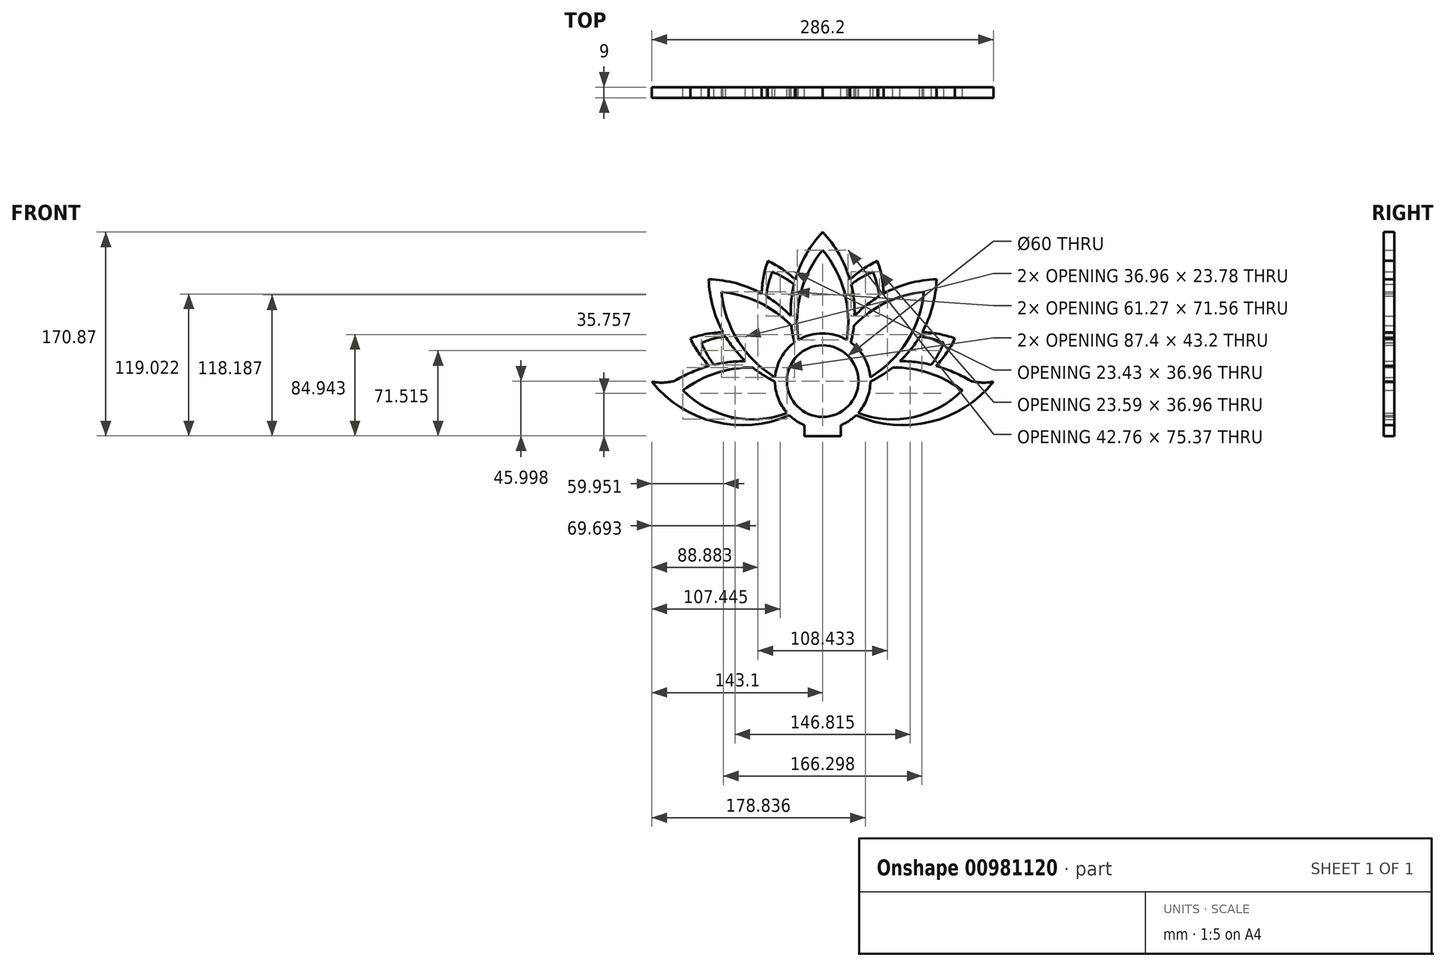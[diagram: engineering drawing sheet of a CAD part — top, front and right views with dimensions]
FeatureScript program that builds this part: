
annotation { "Feature Type Name" : "Feature", "Feature Type Description" : "" }
export const myFeature = defineFeature(function(context is Context, id is Id, definition is map)
    precondition{}
    {
        {
            var Q0;
            Q0=qCreatedBy(makeId("Front.planeOp"),FACE);
            var sketch = newSketch(context, id + "F0", { "sketchPlane" : qUnion([Q0])});
            skCircle(sketch, "E0", {"center": v(0, 0.48) * mm, "radius": 30 * mm});
            skArc(sketch, "E1", {"start": v(0, 110.35) * mm, "mid": v(-18.26, 74.85) * mm, "end": v(-20.24, 34.98) * mm});
            skArc(sketch, "E2", {"start": v(20.24, 34.98) * mm, "mid": v(18.26, 74.85) * mm, "end": v(0, 110.35) * mm});
            skArc(sketch, "E3", {"start": v(84.85, 75.2) * mm, "mid": v(53.03, 66.29) * mm, "end": v(26.22, 46.96) * mm});
            skArc(sketch, "E4", {"start": v(39.87, 3.64) * mm, "mid": v(70.81, 34.11) * mm, "end": v(84.85, 75.2) * mm});
            skArc(sketch, "E5", {"start": v(117.1, -7.36) * mm, "mid": v(89.45, 7.14) * mm, "end": v(58.57, 11.84) * mm});
            skArc(sketch, "E6", {"start": v(29.7, -26.31) * mm, "mid": v(76.2, -29.7) * mm, "end": v(117.1, -7.36) * mm});
            skArc(sketch, "E7", {"start": v(-58.57, 11.84) * mm, "mid": v(-89.45, 7.14) * mm, "end": v(-117.1, -7.36) * mm});
            skArc(sketch, "E8", {"start": v(-117.1, -7.36) * mm, "mid": v(-76.2, -29.7) * mm, "end": v(-29.7, -26.31) * mm});
            skArc(sketch, "E9", {"start": v(-84.85, 75.2) * mm, "mid": v(-70.81, 34.11) * mm, "end": v(-39.87, 3.64) * mm});
            skArc(sketch, "E10", {"start": v(-26.22, 46.96) * mm, "mid": v(-53.03, 66.29) * mm, "end": v(-84.85, 75.2) * mm});
            skArc(sketch, "E11", {"start": v(-101.63, 32.45) * mm, "mid": v(-96.95, 22.91) * mm, "end": v(-91.01, 14.1) * mm});
            skArc(sketch, "E12", {"start": v(-42.1, 91.98) * mm, "mid": v(-45.42, 81.99) * mm, "end": v(-47.37, 71.64) * mm});
            skArc(sketch, "E13", {"start": v(42.1, 91.98) * mm, "mid": v(32.66, 87.36) * mm, "end": v(23.94, 81.51) * mm});
            skArc(sketch, "E14", {"start": v(101.63, 32.45) * mm, "mid": v(91.7, 35.85) * mm, "end": v(81.39, 37.88) * mm});
            skArc(sketch, "E15", {"start": v(47.53, 71.74) * mm, "mid": v(45.5, 82.04) * mm, "end": v(42.1, 91.98) * mm});
            skArc(sketch, "E16", {"start": v(-23.94, 81.51) * mm, "mid": v(-32.66, 87.36) * mm, "end": v(-42.1, 91.98) * mm});
            skArc(sketch, "E17", {"start": v(91.01, 14.1) * mm, "mid": v(96.95, 22.91) * mm, "end": v(101.63, 32.45) * mm});
            skArc(sketch, "E18", {"start": v(-81.39, 37.88) * mm, "mid": v(-91.7, 35.85) * mm, "end": v(-101.63, 32.45) * mm});
            skArc(sketch, "E19", {"start": v(23.58, 32.79) * mm, "mid": v(25.16, 39.83) * mm, "end": v(26.22, 46.96) * mm});
            skArc(sketch, "E20", {"start": v(0, 125.35) * mm, "mid": v(-13.8, 106.75) * mm, "end": v(-22.88, 85.44) * mm});
            skArc(sketch, "E21", {"start": v(-26.79, 55.02) * mm, "mid": v(-36.52, 64.03) * mm, "end": v(-47.37, 71.64) * mm});
            skArc(sketch, "E22", {"start": v(95.46, 85.81) * mm, "mid": v(72.55, 82.42) * mm, "end": v(51.06, 73.77) * mm});
            skArc(sketch, "E23", {"start": v(-95.46, 85.81) * mm, "mid": v(-92.07, 62.9) * mm, "end": v(-83.42, 41.41) * mm});
            skArc(sketch, "E24", {"start": v(29.5, -4.22) * mm, "mid": v(29.57, -4.2) * mm, "end": v(29.64, -4.17) * mm});
            skArc(sketch, "E25", {"start": v(122.93, 1.28) * mm, "mid": v(109.34, 8.12) * mm, "end": v(94.97, 13.1) * mm});
            skArc(sketch, "E26", {"start": v(-143.1, -0.08) * mm, "mid": v(-90.3, -33.76) * mm, "end": v(-27.92, -28.17) * mm});
            skArc(sketch, "E27", {"start": v(27.92, -28.17) * mm, "mid": v(90.3, -33.76) * mm, "end": v(143.1, -0.08) * mm});
            skArc(sketch, "E28", {"start": v(-64.67, 17.14) * mm, "mid": v(-77.93, 16.39) * mm, "end": v(-91.01, 14.1) * mm});
            skArc(sketch, "E29", {"start": v(15.2, -36.52) * mm, "mid": v(21.96, -32.96) * mm, "end": v(27.92, -28.17) * mm});
            skArc(sketch, "E30", {"start": v(45.92, 101.22) * mm, "mid": v(33.78, 94.23) * mm, "end": v(22.88, 85.44) * mm});
            skArc(sketch, "E31", {"start": v(51.06, 73.77) * mm, "mid": v(49.57, 87.7) * mm, "end": v(45.92, 101.22) * mm});
            skArc(sketch, "E32", {"start": v(110.87, 36.27) * mm, "mid": v(97.34, 39.92) * mm, "end": v(83.42, 41.41) * mm});
            skArc(sketch, "E33", {"start": v(94.97, 13.1) * mm, "mid": v(103.83, 24.06) * mm, "end": v(110.87, 36.27) * mm});
            skArc(sketch, "E34", {"start": v(-22.88, 85.44) * mm, "mid": v(-33.78, 94.23) * mm, "end": v(-45.92, 101.22) * mm});
            skArc(sketch, "E35", {"start": v(-45.92, 101.22) * mm, "mid": v(-49.57, 87.7) * mm, "end": v(-51.06, 73.77) * mm});
            skArc(sketch, "E36", {"start": v(-83.42, 41.41) * mm, "mid": v(-97.34, 39.92) * mm, "end": v(-110.87, 36.27) * mm});
            skArc(sketch, "E37", {"start": v(-110.87, 36.27) * mm, "mid": v(-103.83, 24.06) * mm, "end": v(-94.97, 13.1) * mm});
            skArc(sketch, "E38", {"start": v(125.93, 0.11) * mm, "mid": v(134.5, -0.84) * mm, "end": v(143.1, -0.08) * mm});
            skArc(sketch, "E39", {"start": v(-143.1, -0.08) * mm, "mid": v(-134.5, -0.84) * mm, "end": v(-125.93, 0.11) * mm});
            skArc(sketch, "E40", {"start": v(125.93, 0.11) * mm, "mid": v(124.38, 0.57) * mm, "end": v(122.93, 1.28) * mm});
            skArc(sketch, "E41", {"start": v(-122.93, 1.28) * mm, "mid": v(-124.38, 0.57) * mm, "end": v(-125.93, 0.11) * mm});
            skArc(sketch, "E42", {"start": v(-58.57, 11.84) * mm, "mid": v(-49.61, 5.46) * mm, "end": v(-40, 0.13) * mm});
            skArc(sketch, "E43", {"start": v(-81.39, 37.88) * mm, "mid": v(-73.74, 26.94) * mm, "end": v(-64.67, 17.14) * mm});
            skArc(sketch, "E44", {"start": v(-26.22, 46.96) * mm, "mid": v(-25.16, 39.83) * mm, "end": v(-23.58, 32.79) * mm});
            skArc(sketch, "E45", {"start": v(-51.06, 73.77) * mm, "mid": v(-72.55, 82.42) * mm, "end": v(-95.46, 85.81) * mm});
            skArc(sketch, "E46", {"start": v(-23.94, 81.51) * mm, "mid": v(-26.26, 68.37) * mm, "end": v(-26.79, 55.02) * mm});
            skArc(sketch, "E47", {"start": v(22.88, 85.44) * mm, "mid": v(13.8, 106.75) * mm, "end": v(0, 125.35) * mm});
            skArc(sketch, "E48", {"start": v(47.53, 71.74) * mm, "mid": v(36.6, 64.09) * mm, "end": v(26.79, 55.02) * mm});
            skArc(sketch, "E49", {"start": v(26.79, 55.02) * mm, "mid": v(26.26, 68.37) * mm, "end": v(23.94, 81.51) * mm});
            skArc(sketch, "E50", {"start": v(83.42, 41.41) * mm, "mid": v(92.07, 62.9) * mm, "end": v(95.46, 85.81) * mm});
            skArc(sketch, "E51", {"start": v(64.67, 17.14) * mm, "mid": v(73.74, 26.94) * mm, "end": v(81.39, 37.88) * mm});
            skArc(sketch, "E52", {"start": v(-94.97, 13.1) * mm, "mid": v(-109.34, 8.12) * mm, "end": v(-122.93, 1.28) * mm});
            skArc(sketch, "E53", {"start": v(91.01, 14.1) * mm, "mid": v(77.93, 16.39) * mm, "end": v(64.67, 17.14) * mm});
            skLineSegment(sketch, "E54", {"start": v(-15.2, -36.52) * mm, "end": v(-15.2, -45.52) * mm});
            skLineSegment(sketch, "E55", {"start": v(15.2, -36.52) * mm, "end": v(15.2, -45.52) * mm});
            skLineSegment(sketch, "E56", {"start": v(15.2, -45.52) * mm, "end": v(-15.2, -45.52) * mm});
            skArc(sketch, "E57", {"start": v(-29.64, -4.17) * mm, "mid": v(-29.57, -4.2) * mm, "end": v(-29.5, -4.22) * mm});
            skArc(sketch, "E58", {"start": v(40, 0.13) * mm, "mid": v(49.61, 5.46) * mm, "end": v(58.57, 11.84) * mm});
            skArc(sketch, "E59", {"start": v(-27.92, -28.17) * mm, "mid": v(-21.96, -32.96) * mm, "end": v(-15.2, -36.52) * mm});
            skArc(sketch, "E60", {"start": v(29.7, -26.31) * mm, "mid": v(37.27, -14.03) * mm, "end": v(40, 0.13) * mm});
            skArc(sketch, "E61", {"start": v(39.87, 3.64) * mm, "mid": v(34.91, 20) * mm, "end": v(23.58, 32.79) * mm});
            skArc(sketch, "E62", {"start": v(-40, 0.13) * mm, "mid": v(-37.27, -14.03) * mm, "end": v(-29.7, -26.31) * mm});
            skArc(sketch, "E63", {"start": v(-23.58, 32.79) * mm, "mid": v(-34.91, 20) * mm, "end": v(-39.87, 3.64) * mm});
            skArc(sketch, "E64", {"start": v(20.24, 34.98) * mm, "mid": v(0, 40.48) * mm, "end": v(-20.24, 34.98) * mm});
            skLineSegment(sketch, "E65", {"start": v(0, 125.35) * mm, "end": v(0, -45.52) * mm, "construction": true});
            skLineSegment(sketch, "E66", {"start": v(45.92, 101.22) * mm, "end": v(0, -9.65) * mm, "construction": true});
            skLineSegment(sketch, "E67", {"start": v(84.85, 75.2) * mm, "end": v(0, -9.65) * mm, "construction": true});
            skLineSegment(sketch, "E68", {"start": v(110.87, 36.27) * mm, "end": v(0, -9.65) * mm, "construction": true});
            skLineSegment(sketch, "E69", {"start": v(143.1, -0.08) * mm, "end": v(117.1, -7.36) * mm, "construction": true});
            skLineSegment(sketch, "E70", {"start": v(117.1, -7.36) * mm, "end": v(0, -9.65) * mm, "construction": true});
            skSolve(sketch);
        }
        {
            var Q0;
            Q0=makeQuery(id+"F0.imprint","IMPRINT",FACE,{"disambiguationData":[TD([[makeQuery(id+"F0.imprint","IMPRINT",EDGE,{"derivedFrom":sQuery(id+"F0.wireOp",EDGE,"E1")}),-1.0]])]});
            extrude(context, id + "F1", {"entities" : qUnion([Q0]), "endBound" : BoundingType.SYMMETRIC, "depth" : 9 * mm, "offsetDistance" : 25 * mm});
        }
    });
